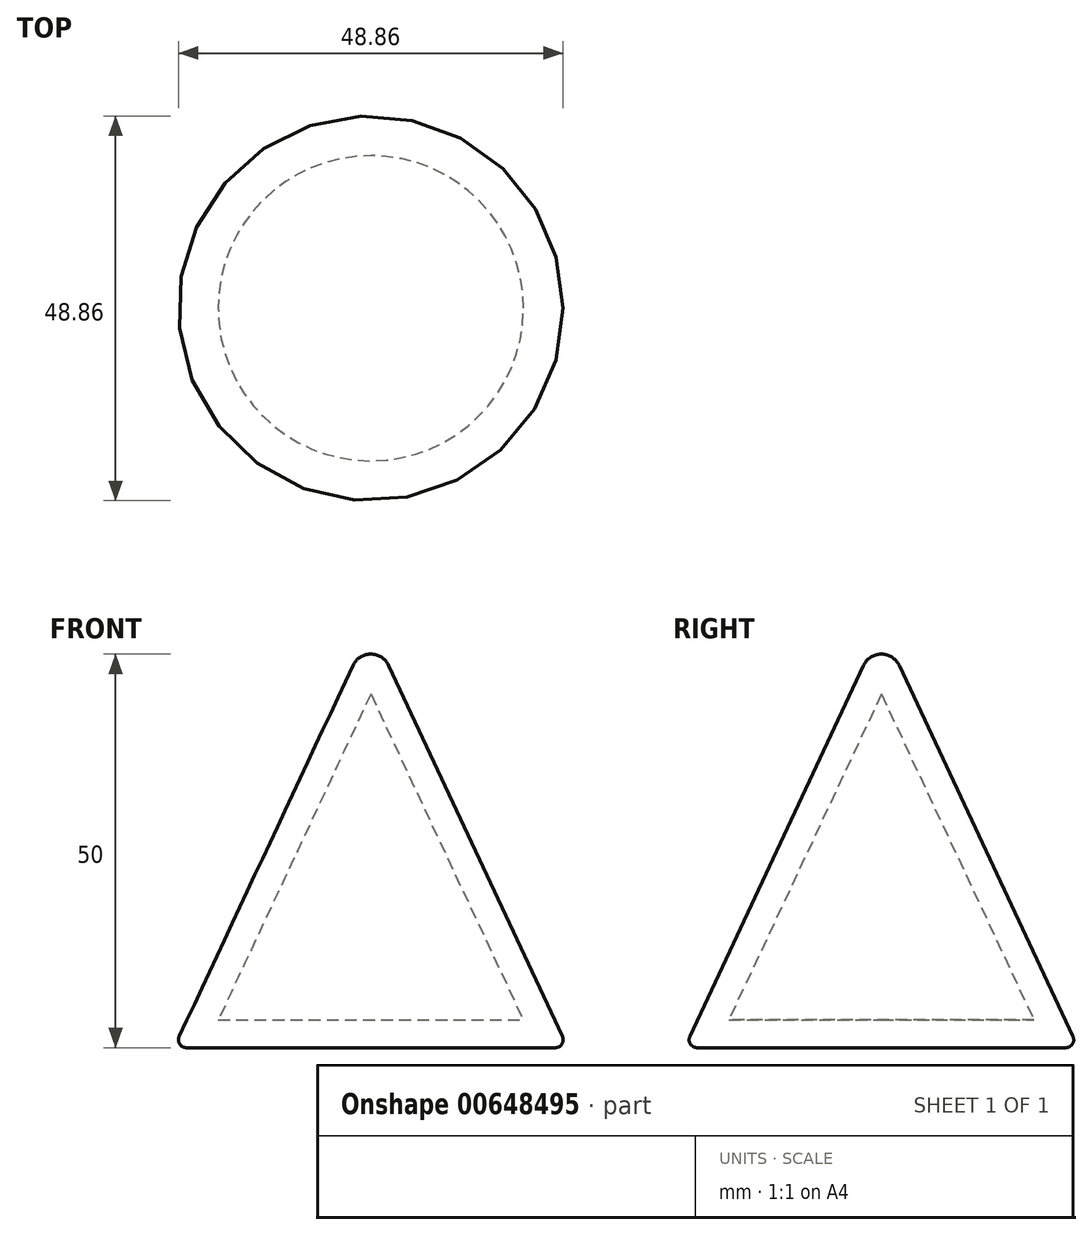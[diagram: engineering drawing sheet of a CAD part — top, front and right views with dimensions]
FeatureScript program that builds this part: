
annotation { "Feature Type Name" : "Feature", "Feature Type Description" : "" }
export const myFeature = defineFeature(function(context is Context, id is Id, definition is map)
    precondition{}
    {
        {
            var Q0;
            Q0=qCreatedBy(makeId("Front.planeOp"),FACE);
            var sketch = newSketch(context, id + "F0", { "sketchPlane" : qUnion([Q0])});
            skLineSegment(sketch, "E0", {"start": v(-2.26, 48.56) * mm, "end": v(-25, 0) * mm});
            skLineSegment(sketch, "E1", {"start": v(-25, 0) * mm, "end": v(0, 0) * mm});
            skLineSegment(sketch, "E2", {"start": v(0, 0) * mm, "end": v(0, 53.4) * mm});
            skLineSegment(sketch, "E3", {"start": v(0, 53.53) * mm, "end": v(0, -16.16) * mm, "construction": true});
            skArc(sketch, "E4", {"start": v(0, 50) * mm, "mid": v(-1.34, 49.6) * mm, "end": v(-2.26, 48.56) * mm});
            skSolve(sketch);
        }
        {
            var Q0;
            Q0=makeQuery(id+"F0.imprint","IMPRINT",FACE,{"disambiguationData":[TD([[makeQuery(id+"F0.imprint","IMPRINT",EDGE,{"derivedFrom":sQuery(id+"F0.wireOp",EDGE,"E0")}),1.0]])]});
            var Q1;
            Q1=sQuery(id+"F0.wireOp",EDGE,"E2");
            revolve(context, id + "F1", {"entities" : qUnion([Q0]), "axis" : qUnion([Q1]), "revolveType" : RevolveType.FULL});
        }
        {
            var Q0;
            Q0=makeQuery(id+"F1.opRevolve","SWEPT_EDGE",EDGE,{"disambiguationData":[OSD([sQuery(id+"F0.wireOp",EDGE,"E0"),sQuery(id+"F0.wireOp",EDGE,"E1")])]});
            fillet(context, id + "F2", {"entities" : qUnion([Q0]), "radius" : 1 * mm, "tangentPropagation" : true, "allowEdgeOverflow" : false});
        }
        {
            var Q0;
            Q0=qCreatedBy(makeId("Front.planeOp"),FACE);
            var sketch = newSketch(context, id + "F3", { "sketchPlane" : qUnion([Q0])});
            skLineSegment(sketch, "E5", {"start": v(0, 44.9) * mm, "end": v(-19.39, 3.5) * mm});
            skLineSegment(sketch, "E6", {"start": v(-19.39, 3.5) * mm, "end": v(0, 3.5) * mm});
            skLineSegment(sketch, "E7", {"start": v(0, 3.5) * mm, "end": v(0, 44.9) * mm});
            skLineSegment(sketch, "E8", {"start": v(-24.33, 1.42) * mm, "end": v(-2.26, 48.56) * mm, "construction": true});
            skLineSegment(sketch, "E9", {"start": v(0, 59.87) * mm, "end": v(0, -10.1) * mm, "construction": true});
            skSolve(sketch);
        }
        {
            var Q0;
            Q0=makeQuery(id+"F3.imprint","IMPRINT",FACE,{"disambiguationData":[TD([[makeQuery(id+"F3.imprint","IMPRINT",EDGE,{"derivedFrom":sQuery(id+"F3.wireOp",EDGE,"E5")}),1.0]])]});
            var Q1;
            Q1=sQuery(id+"F3.wireOp",EDGE,"E9");
            revolve(context, id + "F4", {"operationType" : NewBodyOperationType.REMOVE, "entities" : qUnion([Q0]), "axis" : qUnion([Q1]), "revolveType" : RevolveType.FULL, "oppositeDirection" : true});
        }
    });
